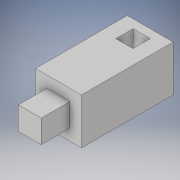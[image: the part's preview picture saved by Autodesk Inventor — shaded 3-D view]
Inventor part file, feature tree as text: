
AUTODESK INVENTOR PART (.ipt)
format: ipt  version: 2019 (Build 230136000, 136)  size: 128,512 bytes
history: native  units: in
note: dims shown in document units (in); Inventor stores cm internally (conversion verified against a paired STEP export)
features: extrude x4, sketch x4
ambient origin geometry x8: Origin, YZ Plane, XZ Plane, XY Plane, X Axis, Y Axis, Z Axis, Center Point
bodies: Solid1 (feature_tree)
feature tree (8):
  extrude  "Extrusion1"  Depth=2.0in
  extrude  "Extrusion2"  Depth=1.0in
  extrude  "Extrusion3"  Depth=1.25in TaperAngle=0.0deg
  extrude  "Extrusion4"  Depth=1.0in
  sketch  "Sketch1"  dims[d0=2.0in d1=2.0in]
  sketch  "Sketch2"  dims[d4=4.0in d5=0.0in d8=1.0in]
  sketch  "Sketch3"  dims[d9=1.0in d10=1.25in d11=0.0in]
  sketch  "Sketch4"  dims[d12=1.0in d13=0.25in d14=0.5in d15=0.25in d16=1.0in d17=0.0in d18=0.125in d19=0.75in d20=0.375in d21=0.75in d22=0.375in d23=1.0in d24=0.0in]
